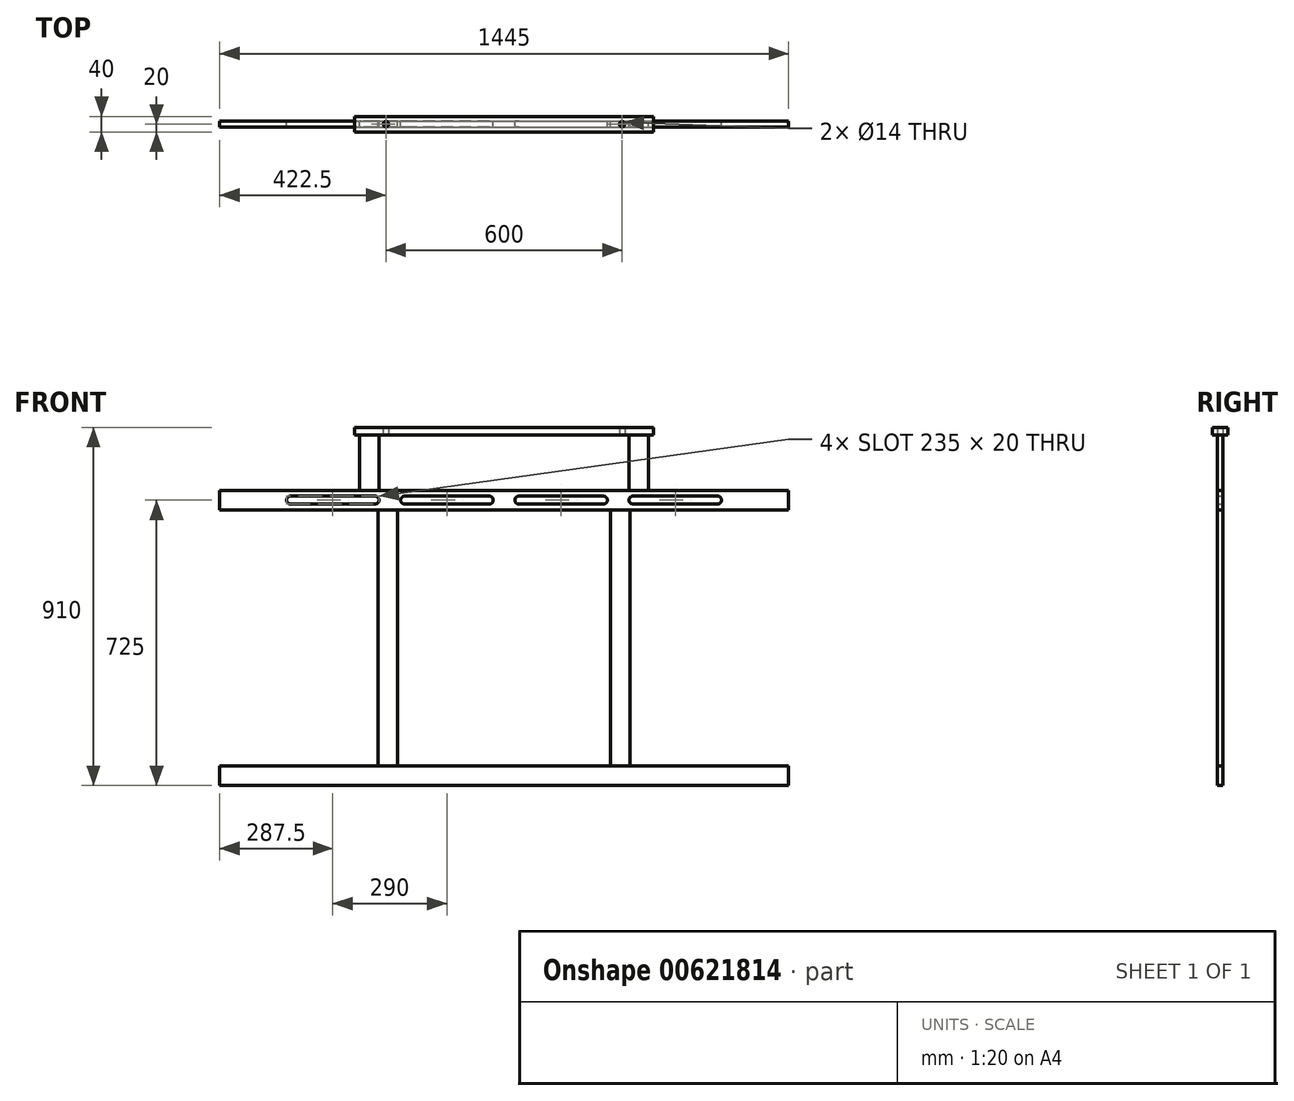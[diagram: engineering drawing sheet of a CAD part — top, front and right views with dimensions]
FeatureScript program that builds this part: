
annotation { "Feature Type Name" : "Feature", "Feature Type Description" : "" }
export const myFeature = defineFeature(function(context is Context, id is Id, definition is map)
    precondition{}
    {
        {
            var Q0;
            Q0=qCreatedBy(makeId("Front.planeOp"),FACE);
            var sketch = newSketch(context, id + "F0", { "sketchPlane" : qUnion([Q0])});
            skLineSegment(sketch, "E0.bottom", {"start": v(270, 0) * mm, "end": v(320, 0) * mm});
            skLineSegment(sketch, "E0.top", {"start": v(270, 650) * mm, "end": v(320, 650) * mm});
            skLineSegment(sketch, "E0.left", {"start": v(270, 0) * mm, "end": v(270, 650) * mm});
            skLineSegment(sketch, "E0.right", {"start": v(320, 0) * mm, "end": v(320, 650) * mm});
            skLineSegment(sketch, "E1.bottom", {"start": v(-270, 650) * mm, "end": v(-320, 650) * mm});
            skLineSegment(sketch, "E1.top", {"start": v(-270, 0) * mm, "end": v(-320, 0) * mm});
            skLineSegment(sketch, "E1.left", {"start": v(-270, 650) * mm, "end": v(-270, 0) * mm});
            skLineSegment(sketch, "E1.right", {"start": v(-320, 650) * mm, "end": v(-320, 0) * mm});
            skLineSegment(sketch, "E2", {"start": v(0, 0) * mm, "end": v(0, 650) * mm, "construction": true});
            skSolve(sketch);
        }
        {
            var Q0;
            Q0=qSketchRegion(id+"F0",true);
            extrude(context, id + "F1", {"entities" : qUnion([Q0]), "depth" : 15 * mm});
        }
        {
            var Q0;
            Q0=qCreatedBy(makeId("Front.planeOp"),FACE);
            var sketch = newSketch(context, id + "F2", { "sketchPlane" : qUnion([Q0])});
            skLineSegment(sketch, "E3.bottom", {"start": v(-722.5, 700) * mm, "end": v(722.5, 700) * mm});
            skLineSegment(sketch, "E3.top", {"start": v(-722.5, 650) * mm, "end": v(722.5, 650) * mm});
            skLineSegment(sketch, "E3.left", {"start": v(-722.5, 700) * mm, "end": v(-722.5, 650) * mm});
            skLineSegment(sketch, "E3.right", {"start": v(722.5, 700) * mm, "end": v(722.5, 650) * mm});
            skLineSegment(sketch, "E4.bottom", {"start": v(722.5, 0) * mm, "end": v(-722.5, 0) * mm});
            skLineSegment(sketch, "E4.top", {"start": v(722.5, -50) * mm, "end": v(-722.5, -50) * mm});
            skLineSegment(sketch, "E4.left", {"start": v(722.5, 0) * mm, "end": v(722.5, -50) * mm});
            skLineSegment(sketch, "E4.right", {"start": v(-722.5, 0) * mm, "end": v(-722.5, -50) * mm});
            skLineSegment(sketch, "E5", {"start": v(0, 0) * mm, "end": v(0, 650) * mm, "construction": true});
            skLineSegment(sketch, "E6.trimOffspring", {"start": v(-722.5, 675) * mm, "end": v(722.5, 675) * mm, "construction": true});
            skLineSegment(sketch, "E7.bottom", {"start": v(-327.5, 685) * mm, "end": v(-542.5, 685) * mm});
            skLineSegment(sketch, "E7.top", {"start": v(-327.5, 665) * mm, "end": v(-542.5, 665) * mm});
            skArc(sketch, "E8", {"start": v(-542.5, 685) * mm, "mid": v(-552.5, 675) * mm, "end": v(-542.5, 665) * mm});
            skArc(sketch, "E9", {"start": v(-327.5, 685) * mm, "mid": v(-317.5, 675) * mm, "end": v(-327.5, 665) * mm});
            skPoint(sketch, "E10", {"position": v(-317.5, 675) * mm});
            skPoint(sketch, "E11.start.orphan", {"position": v(-722.5, 675) * mm});
            skLineSegment(sketch, "E12.1.0.0", {"start": v(-37.5, 665) * mm, "end": v(-252.5, 665) * mm});
            skLineSegment(sketch, "E12.1.0.1", {"start": v(-37.5, 685) * mm, "end": v(-252.5, 685) * mm});
            skArc(sketch, "E12.1.0.3", {"start": v(-37.5, 685) * mm, "mid": v(-27.5, 675) * mm, "end": v(-37.5, 665) * mm});
            skArc(sketch, "E12.1.0.4", {"start": v(-252.5, 685) * mm, "mid": v(-262.5, 675) * mm, "end": v(-252.5, 665) * mm});
            skArc(sketch, "E13.MirrorCS", {"start": v(37.5, 685) * mm, "mid": v(27.5, 675) * mm, "end": v(37.5, 665) * mm});
            skLineSegment(sketch, "E14.MirrorCS", {"start": v(37.5, 665) * mm, "end": v(252.5, 665) * mm});
            skLineSegment(sketch, "E15.MirrorCS", {"start": v(37.5, 685) * mm, "end": v(252.5, 685) * mm});
            skArc(sketch, "E16.MirrorCS", {"start": v(252.5, 685) * mm, "mid": v(262.5, 675) * mm, "end": v(252.5, 665) * mm});
            skArc(sketch, "E17.MirrorCS", {"start": v(327.5, 685) * mm, "mid": v(317.5, 675) * mm, "end": v(327.5, 665) * mm});
            skLineSegment(sketch, "E18.MirrorCS", {"start": v(327.5, 665) * mm, "end": v(542.5, 665) * mm});
            skLineSegment(sketch, "E19.MirrorCS", {"start": v(327.5, 685) * mm, "end": v(542.5, 685) * mm});
            skArc(sketch, "E20.MirrorCS", {"start": v(542.5, 685) * mm, "mid": v(552.5, 675) * mm, "end": v(542.5, 665) * mm});
            skSolve(sketch);
        }
        {
            var Q0;
            Q0=qSketchRegion(id+"F2",true);
            extrude(context, id + "F3", {"entities" : qUnion([Q0]), "depth" : 15 * mm});
        }
        {
            var Q0;
            Q0=qCreatedBy(makeId("Front.planeOp"),FACE);
            var sketch = newSketch(context, id + "F4", { "sketchPlane" : qUnion([Q0])});
            skLineSegment(sketch, "E21.bottom", {"start": v(-317.5, 700) * mm, "end": v(-367.5, 700) * mm});
            skLineSegment(sketch, "E21.top", {"start": v(-317.5, 840) * mm, "end": v(-367.5, 840) * mm});
            skLineSegment(sketch, "E21.left", {"start": v(-317.5, 700) * mm, "end": v(-317.5, 840) * mm});
            skLineSegment(sketch, "E21.right", {"start": v(-367.5, 700) * mm, "end": v(-367.5, 840) * mm});
            skLineSegment(sketch, "E22", {"start": v(0, 840) * mm, "end": v(0, 700) * mm, "construction": true});
            skLineSegment(sketch, "E23.MirrorCS", {"start": v(317.5, 700) * mm, "end": v(317.5, 840) * mm});
            skLineSegment(sketch, "E24.MirrorCS", {"start": v(317.5, 700) * mm, "end": v(367.5, 700) * mm});
            skLineSegment(sketch, "E25.MirrorCS", {"start": v(367.5, 700) * mm, "end": v(367.5, 840) * mm});
            skLineSegment(sketch, "E26.MirrorCS", {"start": v(317.5, 840) * mm, "end": v(367.5, 840) * mm});
            skSolve(sketch);
        }
        {
            var Q0;
            Q0=qSketchRegion(id+"F4",true);
            extrude(context, id + "F5", {"entities" : qUnion([Q0]), "depth" : 15 * mm});
        }
        {
            var Q0;
            Q0=makeQuery(id+"F5.opExtrude","SWEPT_FACE",FACE,{"disambiguationData":[OSD([sQuery(id+"F4.wireOp",EDGE,"E21.top")])]});
            var sketch = newSketch(context, id + "F6", { "sketchPlane" : qUnion([Q0])});
            skLineSegment(sketch, "E27", {"start": v(-722.5, -7.5) * mm, "end": v(722.5, -7.5) * mm, "construction": true});
            skLineSegment(sketch, "E28.bottom", {"start": v(380, -27.5) * mm, "end": v(-380, -27.5) * mm});
            skLineSegment(sketch, "E28.top", {"start": v(380, 12.5) * mm, "end": v(-380, 12.5) * mm});
            skLineSegment(sketch, "E28.left", {"start": v(380, -27.5) * mm, "end": v(380, 12.5) * mm});
            skLineSegment(sketch, "E28.right", {"start": v(-380, -27.5) * mm, "end": v(-380, 12.5) * mm});
            skPoint(sketch, "E28.middle", {"position": v(0, -7.5) * mm});
            skSolve(sketch);
        }
        {
            var Q0;
            Q0=qSketchRegion(id+"F6",true);
            extrude(context, id + "F7", {"entities" : qUnion([Q0]), "depth" : 20 * mm});
        }
        {
            var Q0;
            Q0=makeQuery(id+"F7.opExtrude","CAP_FACE",FACE,{"disambiguationData":[OSD([sQuery(id+"F6.wireOp",EDGE,"E28.bottom"),sQuery(id+"F6.wireOp",EDGE,"E28.top"),sQuery(id+"F6.wireOp",EDGE,"E28.left"),sQuery(id+"F6.wireOp",EDGE,"E28.right")])],"isStart":false});
            var sketch = newSketch(context, id + "F8", { "sketchPlane" : qUnion([Q0])});
            skPoint(sketch, "E29", {"position": v(-300, -7.5) * mm});
            skPoint(sketch, "E30", {"position": v(300, -7.5) * mm});
            skLineSegment(sketch, "E31", {"start": v(-380, -7.5) * mm, "end": v(380, -7.5) * mm, "construction": true});
            skLineSegment(sketch, "E32", {"start": v(0, -27.5) * mm, "end": v(0, 12.5) * mm, "construction": true});
            skSolve(sketch);
        }
        {
            var Q0;
            Q0=sQuery(id+"F8.wireOp",VERTEX,"E29");
            var Q1;
            Q1=sQuery(id+"F8.wireOp",VERTEX,"E30");
            var Q2;
            Q2=makeQuery(id+"F7.opExtrude","SWEPT_BODY",BODY,{"disambiguationData":[OSD([sQuery(id+"F6.wireOp",EDGE,"E28.bottom"),sQuery(id+"F6.wireOp",EDGE,"E28.top"),sQuery(id+"F6.wireOp",EDGE,"E28.left"),sQuery(id+"F6.wireOp",EDGE,"E28.right")])]});
            hole(context, id + "F9", {"style" : HoleStyle.SIMPLE, "endStyle" : HoleEndStyle.THROUGH, "standardTappedOrClearance" : lookupTablePath({ "standard" : "ISO", "engagement" : "75%", "pitch" : "2 mm", "size" : "M16", "type" : "Tapped" }), "standardBlindInLast" : lookupTablePath({ "standard" : "ISO", "engagement" : "75%", "pitch" : "2 mm", "size" : "M16", "type" : "Tapped" }), "holeDiameter" : 14 * mm, "locations" : qUnion([Q0, Q1]), "scope" : qUnion([Q2]), "isTappedThrough" : true, "majorDiameter" : 16 * mm, "showTappedDepth" : true});
        }
    });
